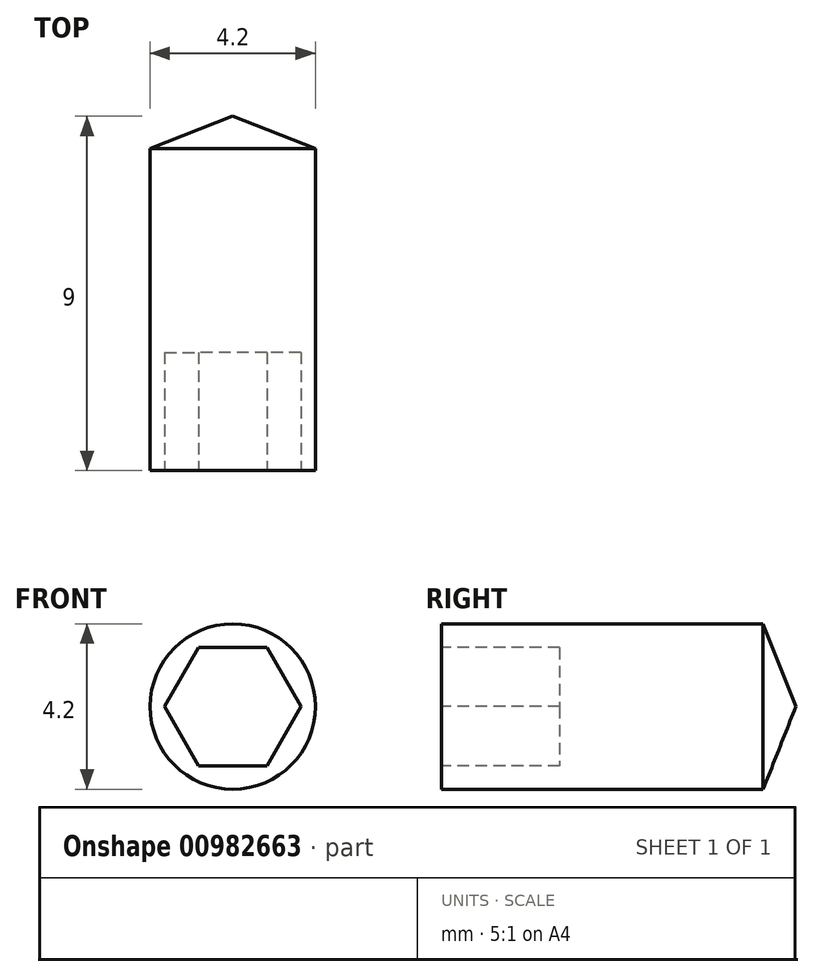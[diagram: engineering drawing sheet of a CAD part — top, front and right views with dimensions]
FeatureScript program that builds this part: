
annotation { "Feature Type Name" : "Feature", "Feature Type Description" : "" }
export const myFeature = defineFeature(function(context is Context, id is Id, definition is map)
    precondition{}
    {
        {
            var Q0;
            Q0=qCreatedBy(makeId("Top.planeOp"),FACE);
            var sketch = newSketch(context, id + "F0", { "sketchPlane" : qUnion([Q0])});
            skLineSegment(sketch, "E0", {"start": v(0, 6.33) * mm, "end": v(0, -6.17) * mm, "construction": true});
            skLineSegment(sketch, "E1.top", {"start": v(0, -5.86) * mm, "end": v(2.1, -5.86) * mm});
            skLineSegment(sketch, "E1.left", {"start": v(0, 3.14) * mm, "end": v(0, -5.86) * mm});
            skLineSegment(sketch, "E1.right", {"start": v(2.1, 2.31) * mm, "end": v(2.1, -5.86) * mm});
            skLineSegment(sketch, "E2", {"start": v(0, 3.14) * mm, "end": v(2.1, 2.31) * mm});
            skSolve(sketch);
        }
        {
            var Q0;
            Q0=makeQuery(id+"F0.imprint","IMPRINT",FACE,{"disambiguationData":[TD([[makeQuery(id+"F0.imprint","IMPRINT",EDGE,{"derivedFrom":sQuery(id+"F0.wireOp",EDGE,"E1.top")}),1.0]])]});
            var Q1;
            Q1=sQuery(id+"F0.wireOp",EDGE,"E0");
            revolve(context, id + "F1", {"surfaceOperationType" : NewSurfaceOperationType.NEW, "entities" : qUnion([Q0]), "axis" : qUnion([Q1]), "revolveType" : RevolveType.FULL});
        }
        {
            var Q0;
            Q0=makeQuery(id+"F1.opRevolve","SWEPT_FACE",FACE,{"disambiguationData":[OSD([sQuery(id+"F0.wireOp",EDGE,"E1.top")])]});
            var sketch = newSketch(context, id + "F2", { "sketchPlane" : qUnion([Q0])});
            skCircle(sketch, "E3.cCircle", {"center": v(0, 0) * mm, "radius": 1.5 * mm, "construction": true});
            skLineSegment(sketch, "E3.0", {"start": v(0.87, -1.5) * mm, "end": v(-0.87, -1.5) * mm});
            skLineSegment(sketch, "E3.1", {"start": v(-0.87, -1.5) * mm, "end": v(-1.73, 0) * mm});
            skLineSegment(sketch, "E3.2", {"start": v(-1.73, 0) * mm, "end": v(-0.87, 1.5) * mm});
            skLineSegment(sketch, "E3.3", {"start": v(-0.87, 1.5) * mm, "end": v(0.87, 1.5) * mm});
            skLineSegment(sketch, "E3.4", {"start": v(0.87, 1.5) * mm, "end": v(1.73, 0) * mm});
            skLineSegment(sketch, "E3.5", {"start": v(1.73, 0) * mm, "end": v(0.87, -1.5) * mm});
            skPoint(sketch, "E3.0.midPoint", {"position": v(0, -1.5) * mm});
            skSolve(sketch);
        }
        {
            var Q0;
            Q0=makeQuery(id+"F2.imprint","IMPRINT",FACE,{"disambiguationData":[TD([[makeQuery(id+"F2.imprint","IMPRINT",EDGE,{"derivedFrom":sQuery(id+"F2.wireOp",EDGE,"E3.0")}),-1.0]])]});
            extrude(context, id + "F3", {"entities" : qUnion([Q0]), "operationType" : NewBodyOperationType.REMOVE, "oppositeDirection" : true, "depth" : 3 * mm, "offsetDistance" : 25 * mm});
        }
    });
